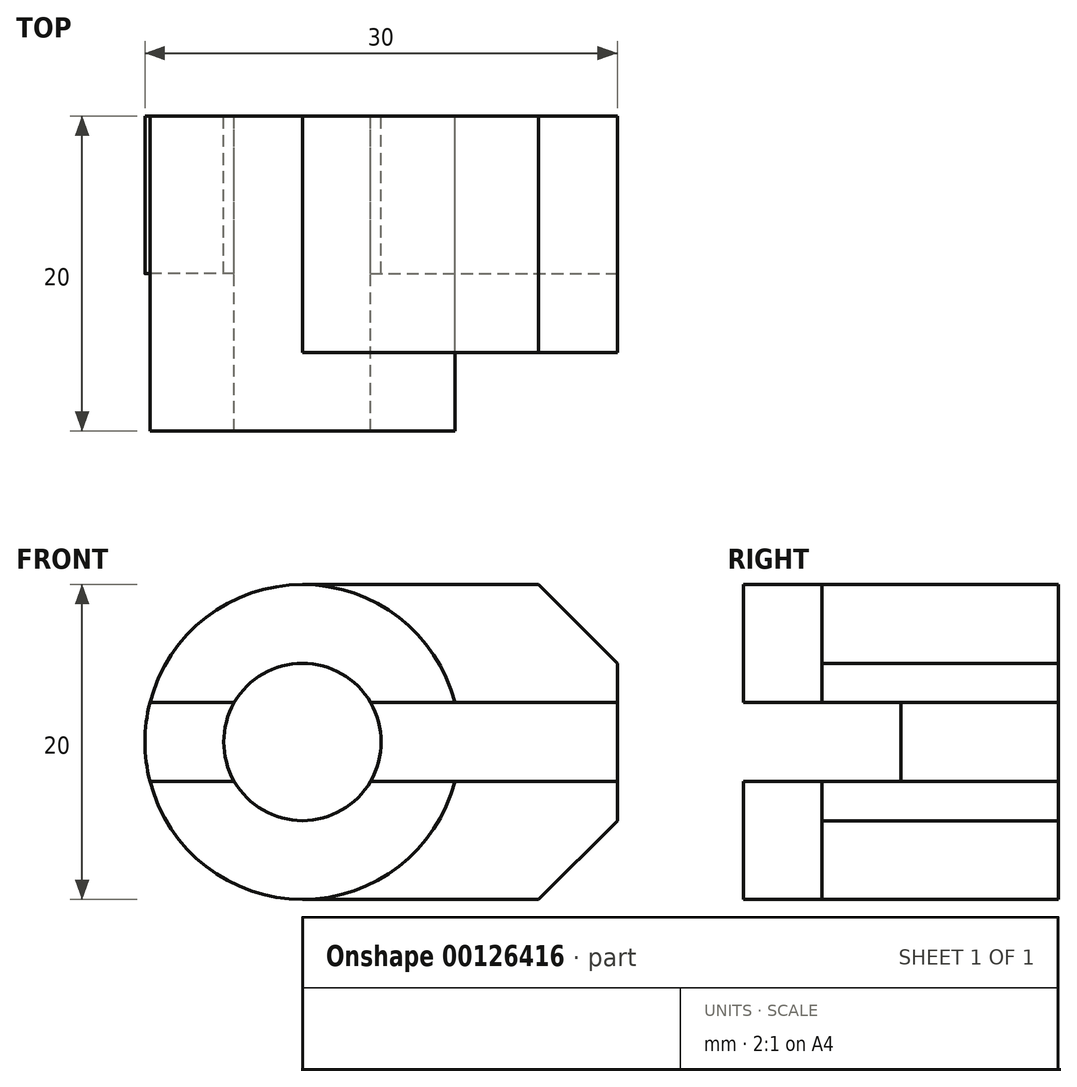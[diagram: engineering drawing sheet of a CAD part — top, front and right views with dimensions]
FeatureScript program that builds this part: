
annotation { "Feature Type Name" : "Feature", "Feature Type Description" : "" }
export const myFeature = defineFeature(function(context is Context, id is Id, definition is map)
    precondition{}
    {
        {
            var Q0;
            Q0=qCreatedBy(makeId("Front.planeOp"),FACE);
            var sketch = newSketch(context, id + "F0", { "sketchPlane" : qUnion([Q0])});
            skCircle(sketch, "E0", {"center": v(0, 0) * mm, "radius": 5 * mm});
            skLineSegment(sketch, "E1", {"start": v(-4.33, 2.5) * mm, "end": v(-9.68, 2.5) * mm});
            skLineSegment(sketch, "E2", {"start": v(-9.68, -2.5) * mm, "end": v(-4.33, -2.5) * mm});
            skLineSegment(sketch, "E3", {"start": v(4.33, 2.5) * mm, "end": v(20, 2.5) * mm});
            skLineSegment(sketch, "E4", {"start": v(20, 2.5) * mm, "end": v(20, -2.5) * mm});
            skLineSegment(sketch, "E5", {"start": v(20, -2.5) * mm, "end": v(4.33, -2.5) * mm});
            skLineSegment(sketch, "E6", {"start": v(0, 10) * mm, "end": v(15, 10) * mm});
            skLineSegment(sketch, "E7", {"start": v(0, -10) * mm, "end": v(15, -10) * mm});
            skLineSegment(sketch, "E8", {"start": v(20, 2.5) * mm, "end": v(20, 5) * mm});
            skLineSegment(sketch, "E9", {"start": v(20, 5) * mm, "end": v(15, 10) * mm});
            skLineSegment(sketch, "E10", {"start": v(20, -2.5) * mm, "end": v(20, -5) * mm});
            skLineSegment(sketch, "E11", {"start": v(20, -5) * mm, "end": v(15, -10) * mm});
            skArc(sketch, "E12", {"start": v(9.68, 2.5) * mm, "mid": v(-10, 0) * mm, "end": v(9.68, -2.5) * mm});
            skSolve(sketch);
        }
        {
            var Q0;
            {var subQ6=sQuery(id+"F0.wireOp",EDGE,"E1");Q0=makeQuery(id+"F0.imprint","IMPRINT",FACE,{"disambiguationData":[TD([[makeQuery(id+"F0.imprint","IMPRINT",EDGE,{"derivedFrom":subQ6}),-1.0]])]});}
            var Q1;
            {var subQ5=sQuery(id+"F0.wireOp",EDGE,"E2");Q1=makeQuery(id+"F0.imprint","IMPRINT",FACE,{"disambiguationData":[TD([[makeQuery(id+"F0.imprint","IMPRINT",EDGE,{"derivedFrom":subQ5}),-1.0]])]});}
            extrude(context, id + "F1", {"entities" : qUnion([Q0, Q1]), "depth" : 20 * mm});
        }
        {
            var Q0;
            {var subQ0=sQuery(id+"F0.wireOp",EDGE,"E1");Q0=makeQuery(id+"F0.imprint","IMPRINT",FACE,{"disambiguationData":[TD([[makeQuery(id+"F0.imprint","IMPRINT",EDGE,{"derivedFrom":subQ0}),1.0]])]});}
            var Q1;
            {var subQ0=sQuery(id+"F0.wireOp",EDGE,"E4");Q1=makeQuery(id+"F0.imprint","IMPRINT",FACE,{"disambiguationData":[TD([[makeQuery(id+"F0.imprint","IMPRINT",EDGE,{"derivedFrom":subQ0}),-1.0]])]});}
            extrude(context, id + "F2", {"entities" : qUnion([Q0, Q1]), "depth" : 10 * mm});
        }
        {
            var Q0;
            {var subQ4=sQuery(id+"F0.wireOp",EDGE,"E6");Q0=makeQuery(id+"F0.imprint","IMPRINT",FACE,{"disambiguationData":[TD([[makeQuery(id+"F0.imprint","IMPRINT",EDGE,{"derivedFrom":subQ4}),-1.0]])]});}
            var Q1;
            {var subQ0=sQuery(id+"F0.wireOp",EDGE,"E7");Q1=makeQuery(id+"F0.imprint","IMPRINT",FACE,{"disambiguationData":[TD([[makeQuery(id+"F0.imprint","IMPRINT",EDGE,{"derivedFrom":subQ0}),1.0]])]});}
            extrude(context, id + "F3", {"entities" : qUnion([Q0, Q1]), "depth" : 15 * mm});
        }
    });
